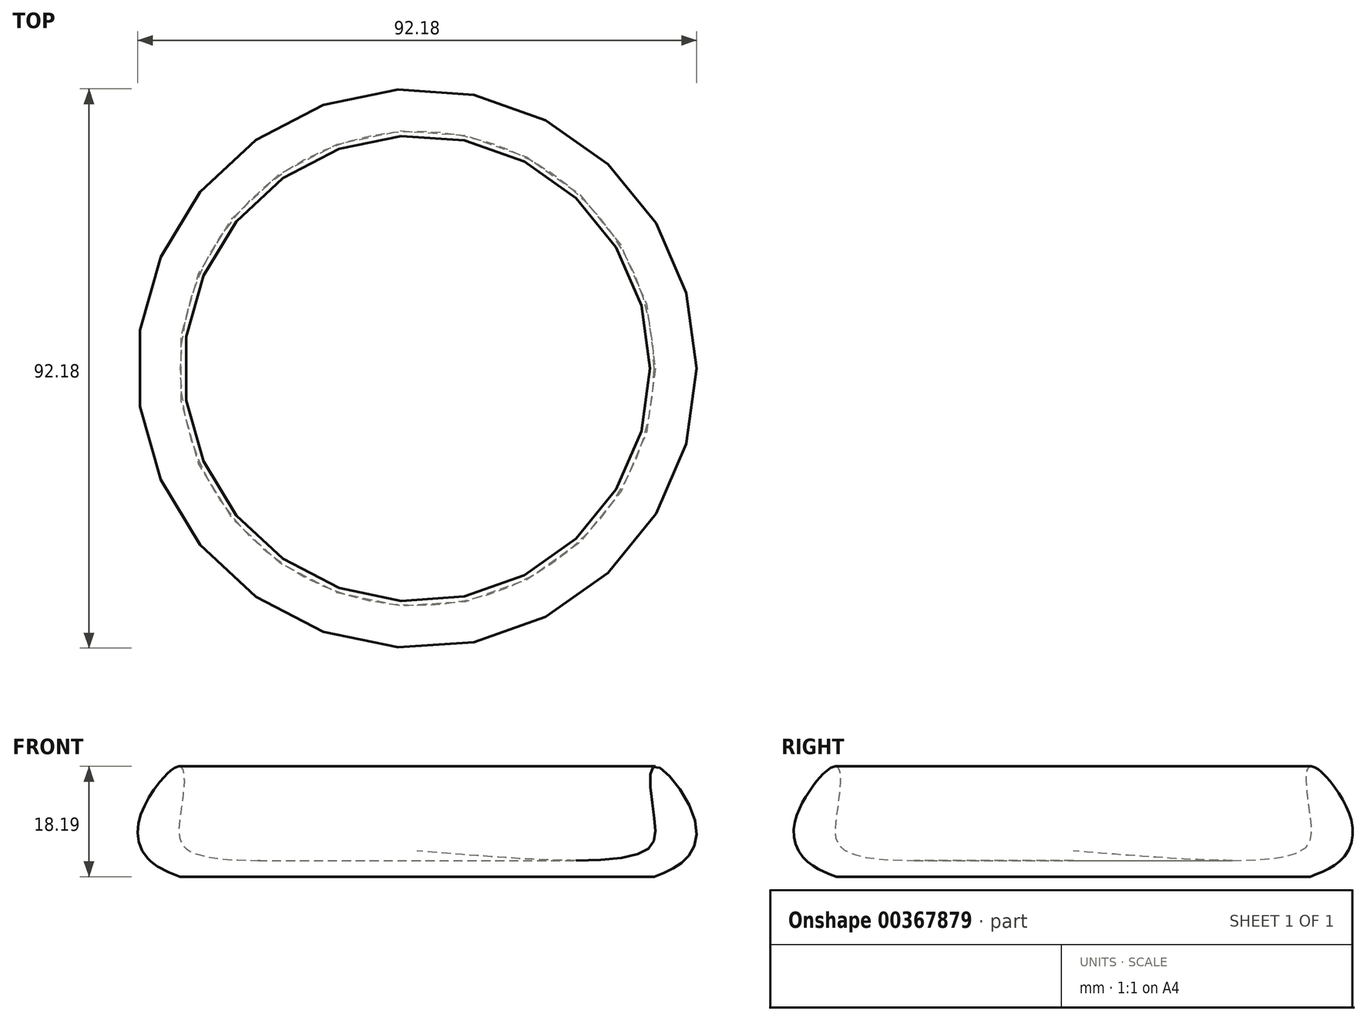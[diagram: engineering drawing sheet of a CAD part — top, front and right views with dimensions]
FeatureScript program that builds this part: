
annotation { "Feature Type Name" : "Feature", "Feature Type Description" : "" }
export const myFeature = defineFeature(function(context is Context, id is Id, definition is map)
    precondition{}
    {
        {
            var Q0;
            Q0=qCreatedBy(makeId("Front.planeOp"),FACE);
            var sketch = newSketch(context, id + "F0", { "sketchPlane" : qUnion([Q0])});
            skLineSegment(sketch, "E0", {"start": v(0, 4.26) * mm, "end": v(0, 0) * mm});
            skLineSegment(sketch, "E1", {"start": v(0, 0) * mm, "end": v(39.06, 0) * mm});
            skFitSpline(sketch, "E2", {"points": [v(39.06, 0) * mm, v(44.08, 2.7) * mm, v(45.74, 9.65) * mm, v(39.06, 18.16) * mm, v(39.06, 9.96) * mm, v(37.74, 4.35) * mm, v(0, 4.26) * mm], "startDerivative": vector(45, 16.84) * mm, "endDerivative": vector(-160.3, 13.4) * mm});
            skPoint(sketch, "E3.orphan", {"position": v(0, 34.07) * mm});
            skPoint(sketch, "E4.orphan", {"position": v(0, -25.55) * mm});
            skSolve(sketch);
        }
        {
            var Q0;
            Q0=makeQuery(id+"F0.imprint","IMPRINT",FACE,{"disambiguationData":[TD([[makeQuery(id+"F0.imprint","IMPRINT",EDGE,{"derivedFrom":sQuery(id+"F0.wireOp",EDGE,"E0")}),1.0]])]});
            var Q1;
            Q1=sQuery(id+"F0.wireOp",EDGE,"E0");
            revolve(context, id + "F1", {"entities" : qUnion([Q0]), "axis" : qUnion([Q1]), "revolveType" : RevolveType.FULL});
        }
    });
